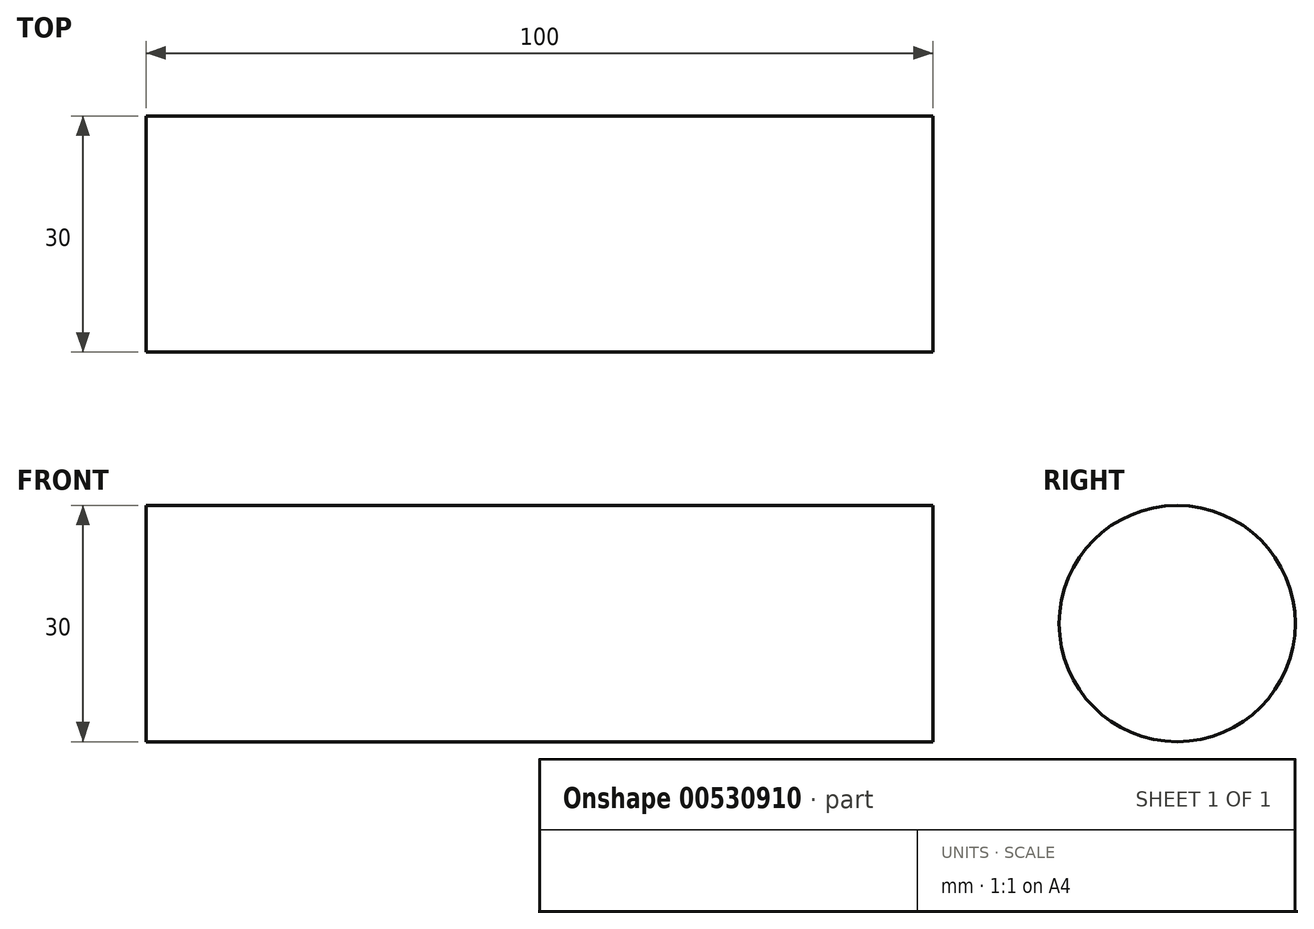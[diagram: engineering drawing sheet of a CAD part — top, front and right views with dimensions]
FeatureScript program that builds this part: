
annotation { "Feature Type Name" : "Feature", "Feature Type Description" : "" }
export const myFeature = defineFeature(function(context is Context, id is Id, definition is map)
    precondition{}
    {
        {
            var Q0;
            Q0=qCreatedBy(makeId("Front.planeOp"),FACE);
            var sketch = newSketch(context, id + "F0", { "sketchPlane" : qUnion([Q0])});
            skLineSegment(sketch, "E0.bottom", {"start": v(0, 15) * mm, "end": v(100, 15) * mm});
            skLineSegment(sketch, "E0.top", {"start": v(0, 0) * mm, "end": v(100, 0) * mm});
            skLineSegment(sketch, "E0.left", {"start": v(0, 15) * mm, "end": v(0, 0) * mm});
            skLineSegment(sketch, "E0.right", {"start": v(100, 15) * mm, "end": v(100, 0) * mm});
            skLineSegment(sketch, "E1", {"start": v(135.13, 0) * mm, "end": v(-136.13, 0) * mm, "construction": true});
            skSolve(sketch);
        }
        {
            var Q0;
            Q0=makeQuery(id+"F0.imprint","IMPRINT",FACE,{"disambiguationData":[TD([[makeQuery(id+"F0.imprint","IMPRINT",EDGE,{"derivedFrom":sQuery(id+"F0.wireOp",EDGE,"E0.bottom")}),-1.0]])]});
            var Q1;
            Q1=sQuery(id+"F0.wireOp",EDGE,"E1");
            revolve(context, id + "F1", {"entities" : qUnion([Q0]), "axis" : qUnion([Q1]), "revolveType" : RevolveType.FULL});
        }
    });
